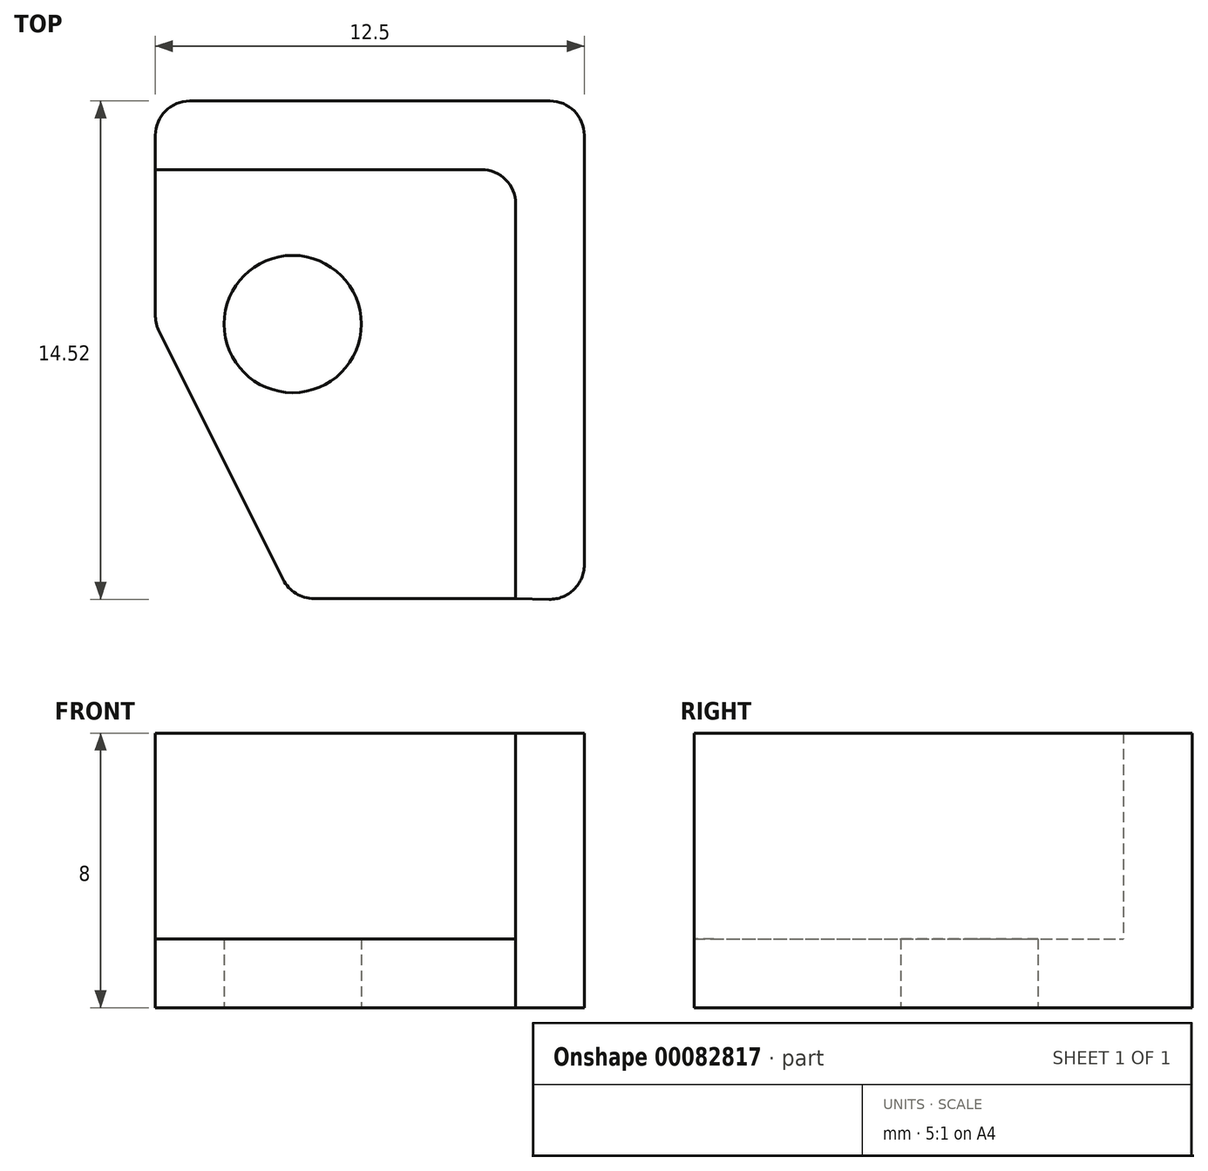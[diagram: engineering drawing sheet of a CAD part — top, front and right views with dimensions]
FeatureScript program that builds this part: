
annotation { "Feature Type Name" : "Feature", "Feature Type Description" : "" }
export const myFeature = defineFeature(function(context is Context, id is Id, definition is map)
    precondition{}
    {
        {
            var Q0;
            Q0=qCreatedBy(makeId("Top.planeOp"),FACE);
            var sketch = newSketch(context, id + "F0", { "sketchPlane" : qUnion([Q0])});
            skCircle(sketch, "E0", {"center": v(0, 0) * mm, "radius": 2 * mm});
            skLineSegment(sketch, "E1", {"start": v(-4, 0) * mm, "end": v(-4, 4.5) * mm});
            skLineSegment(sketch, "E2", {"start": v(-4, 4.5) * mm, "end": v(6.5, 4.5) * mm});
            skLineSegment(sketch, "E3", {"start": v(6.5, 4.5) * mm, "end": v(6.5, -8) * mm});
            skLineSegment(sketch, "E4", {"start": v(6.5, -8) * mm, "end": v(0, -8) * mm});
            skLineSegment(sketch, "E5", {"start": v(0, -8) * mm, "end": v(-4, 0) * mm});
            skLineSegment(sketch, "E6", {"start": v(-4, 4.5) * mm, "end": v(-4, 6.5) * mm});
            skLineSegment(sketch, "E7", {"start": v(-4, 6.5) * mm, "end": v(8.5, 6.5) * mm});
            skLineSegment(sketch, "E8", {"start": v(8.5, 6.5) * mm, "end": v(8.5, -8.04) * mm});
            skLineSegment(sketch, "E9", {"start": v(8.5, -8.04) * mm, "end": v(6.5, -8) * mm});
            skSolve(sketch);
        }
        {
            var Q0;
            Q0=makeQuery(id+"F0.imprint","IMPRINT",FACE,{"disambiguationData":[TD([[makeQuery(id+"F0.imprint","IMPRINT",EDGE,{"derivedFrom":sQuery(id+"F0.wireOp",EDGE,"E0")}),-1.0]])]});
            var Q1;
            Q1=makeQuery(id+"F0.imprint","IMPRINT",FACE,{"disambiguationData":[TD([[makeQuery(id+"F0.imprint","IMPRINT",EDGE,{"derivedFrom":sQuery(id+"F0.wireOp",EDGE,"E2")}),1.0]])]});
            extrude(context, id + "F1", {"entities" : qUnion([Q0, Q1]), "depth" : 2 * mm});
        }
        {
            var Q0;
            Q0=makeQuery(id+"F0.imprint","IMPRINT",FACE,{"disambiguationData":[TD([[makeQuery(id+"F0.imprint","IMPRINT",EDGE,{"derivedFrom":sQuery(id+"F0.wireOp",EDGE,"E2")}),1.0]])]});
            extrude(context, id + "F2", {"entities" : qUnion([Q0]), "operationType" : NewBodyOperationType.ADD, "depth" : 8 * mm});
        }
        {
            var Q0;
            Q0=makeQuery(id+"F2.opExtrude","SWEPT_EDGE",EDGE,{"disambiguationData":[OSD([sQuery(id+"F0.wireOp",EDGE,"E2"),sQuery(id+"F0.wireOp",EDGE,"E3")])]});
            var Q1;
            {var subQ0=sQuery(id+"F0.wireOp",EDGE,"E8");var subQ1=sQuery(id+"F0.wireOp",EDGE,"E7");Q1=makeQuery(id+"F2.boolean.opBoolean","MERGE",EDGE,{"derivedFrom":[makeQuery(id+"F1.opExtrude","SWEPT_EDGE",EDGE,{"disambiguationData":[OSD([subQ1,subQ0])]}),makeQuery(id+"F2.opExtrude","SWEPT_EDGE",EDGE,{"disambiguationData":[OSD([subQ1,subQ0])]})]});}
            var Q2;
            {var subQ0=sQuery(id+"F0.wireOp",EDGE,"E7");var subQ1=sQuery(id+"F0.wireOp",EDGE,"E6");Q2=makeQuery(id+"F2.boolean.opBoolean","MERGE",EDGE,{"derivedFrom":[makeQuery(id+"F1.opExtrude","SWEPT_EDGE",EDGE,{"disambiguationData":[OSD([subQ1,subQ0])]}),makeQuery(id+"F2.opExtrude","SWEPT_EDGE",EDGE,{"disambiguationData":[OSD([subQ1,subQ0])]})]});}
            var Q3;
            Q3=makeQuery(id+"F1.opExtrude","SWEPT_EDGE",EDGE,{"disambiguationData":[OSD([sQuery(id+"F0.wireOp",EDGE,"E1"),sQuery(id+"F0.wireOp",EDGE,"E5")])]});
            var Q4;
            Q4=makeQuery(id+"F1.opExtrude","SWEPT_EDGE",EDGE,{"disambiguationData":[OSD([sQuery(id+"F0.wireOp",EDGE,"E4"),sQuery(id+"F0.wireOp",EDGE,"E5")])]});
            var Q5;
            {var subQ0=sQuery(id+"F0.wireOp",EDGE,"E9");var subQ1=sQuery(id+"F0.wireOp",EDGE,"E8");Q5=makeQuery(id+"F2.boolean.opBoolean","MERGE",EDGE,{"derivedFrom":[makeQuery(id+"F1.opExtrude","SWEPT_EDGE",EDGE,{"disambiguationData":[OSD([subQ1,subQ0])]}),makeQuery(id+"F2.opExtrude","SWEPT_EDGE",EDGE,{"disambiguationData":[OSD([subQ1,subQ0])]})]});}
            fillet(context, id + "F3", {"entities" : qUnion([Q0, Q1, Q2, Q3, Q4, Q5]), "radius" : 1 * mm, "tangentPropagation" : true, "allowEdgeOverflow" : false});
        }
    });
